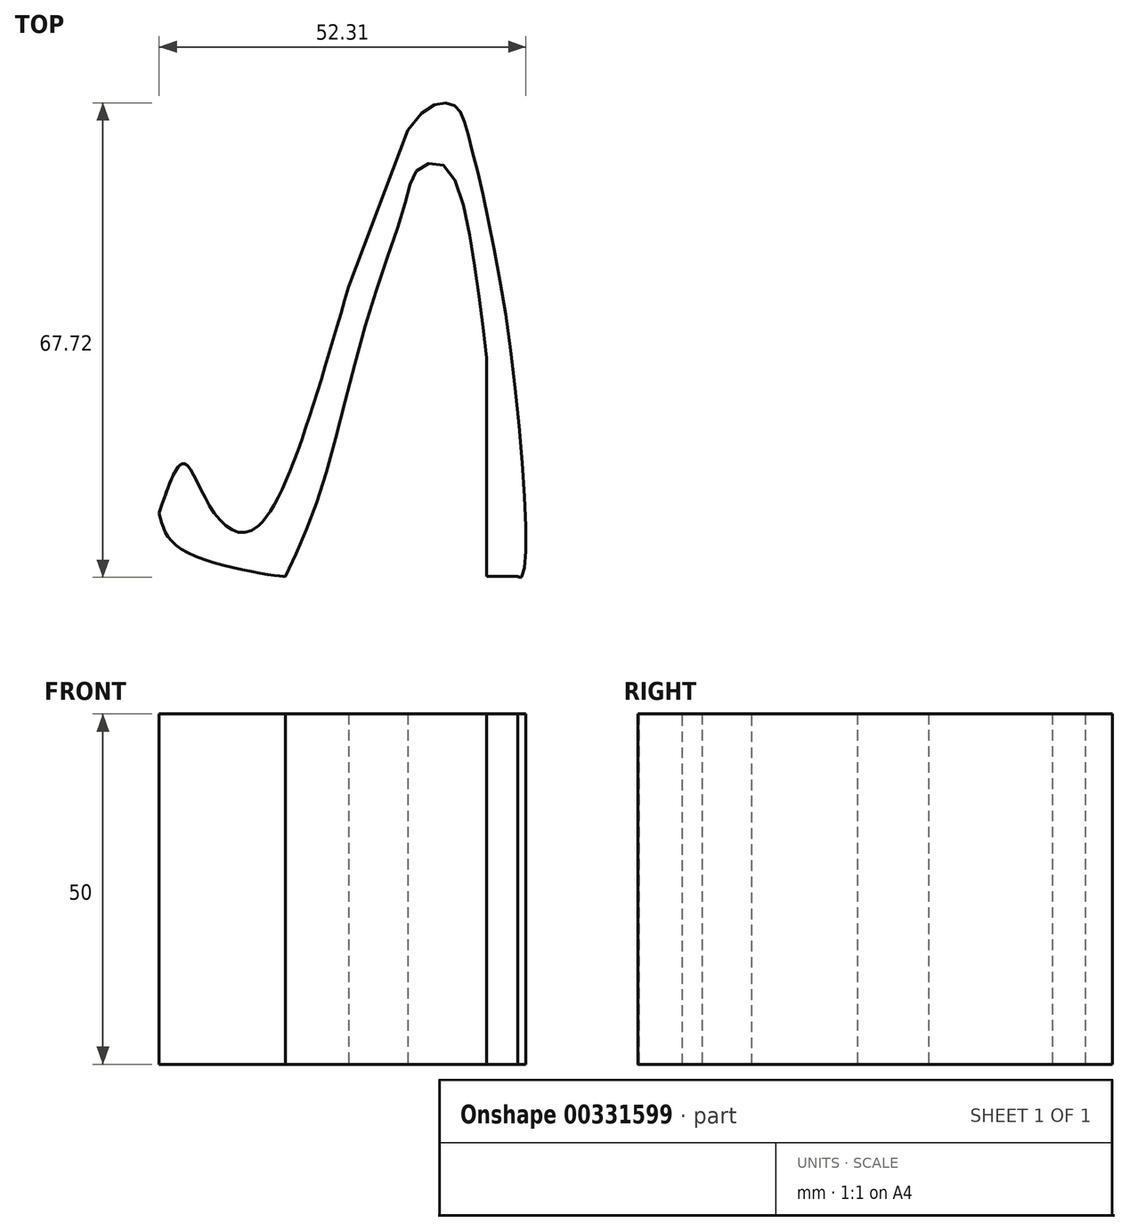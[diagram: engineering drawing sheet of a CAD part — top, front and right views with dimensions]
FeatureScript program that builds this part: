
annotation { "Feature Type Name" : "Feature", "Feature Type Description" : "" }
export const myFeature = defineFeature(function(context is Context, id is Id, definition is map)
    precondition{}
    {
        {
            var Q0;
            Q0=qCreatedBy(makeId("Top.planeOp"),FACE);
            var sketch = newSketch(context, id + "F0", { "sketchPlane" : qUnion([Q0])});
            skFitSpline(sketch, "E0", {"points": [v(0, 9.02) * mm, v(3.55, 16.12) * mm, v(7.7, 9.32) * mm, v(14.2, 7.25) * mm, v(35.5, 63.74) * mm, v(42, 67.3) * mm, v(44.07, 63.15) * mm, v(49.99, 33.57) * mm, v(51.76, 0) * mm, v(51.17, 0) * mm], "startDerivative": vector(42.04, 126.9) * mm, "endDerivative": vector(-27.14, 12.32) * mm});
            skFitSpline(sketch, "E1", {"points": [v(0, 9.02) * mm, v(3.55, 3.7) * mm, v(17.75, 0) * mm, v(18.04, 0) * mm], "startDerivative": vector(3.85, -15.66) * mm, "endDerivative": vector(1.85, 0.3) * mm});
            skLineSegment(sketch, "E2", {"start": v(51.76, 0) * mm, "end": v(46.73, 0) * mm});
            skFitSpline(sketch, "E3", {"points": [v(18.04, 0) * mm, v(23.07, 12.28) * mm, v(29.58, 36.23) * mm, v(35.2, 53.69) * mm, v(36.97, 58.12) * mm, v(40.52, 58.71) * mm, v(44.37, 48.36) * mm, v(46.73, 31.2) * mm], "startDerivative": vector(34.7, 74.16) * mm, "endDerivative": vector(12.03, -100.74) * mm});
            skFitSpline(sketch, "E4", {"points": [v(46.73, 31.2) * mm, v(46.73, 0) * mm], "startDerivative": vector(0, -31.2) * mm, "endDerivative": vector(0, -31.2) * mm});
            skLineSegment(sketch, "E5", {"start": v(14.2, 7.25) * mm, "end": v(35.5, 63.74) * mm});
            skSolve(sketch);
        }
        {
            var Q0;
            {var subQ0=sQuery(id+"F0.wireOp",EDGE,"E2");var subQ1=sQuery(id+"F0.wireOp",EDGE,"E0");var subQ2=makeQuery(id+"F0.imprint","INTERSECT",VERTEX,{"disambiguationData":[OD(0.0)],"derivedFrom":[subQ1,subQ0]});Q0=makeQuery(id+"F0.imprint","IMPRINT",FACE,{"disambiguationData":[TD([[makeQuery(id+"F0.imprint","IMPRINT",EDGE,{"disambiguationData":[TD([[subQ2,1.0]])],"derivedFrom":subQ1}),-1.0]])]});}
            var Q1;
            {var subQ5=sQuery(id+"F0.wireOp",EDGE,"E1");Q1=makeQuery(id+"F0.imprint","IMPRINT",FACE,{"disambiguationData":[TD([[makeQuery(id+"F0.imprint","IMPRINT",EDGE,{"derivedFrom":subQ5}),1.0]])]});}
            extrude(context, id + "F1", {"entities" : qUnion([Q0, Q1]), "depth" : 50 * mm});
        }
    });
